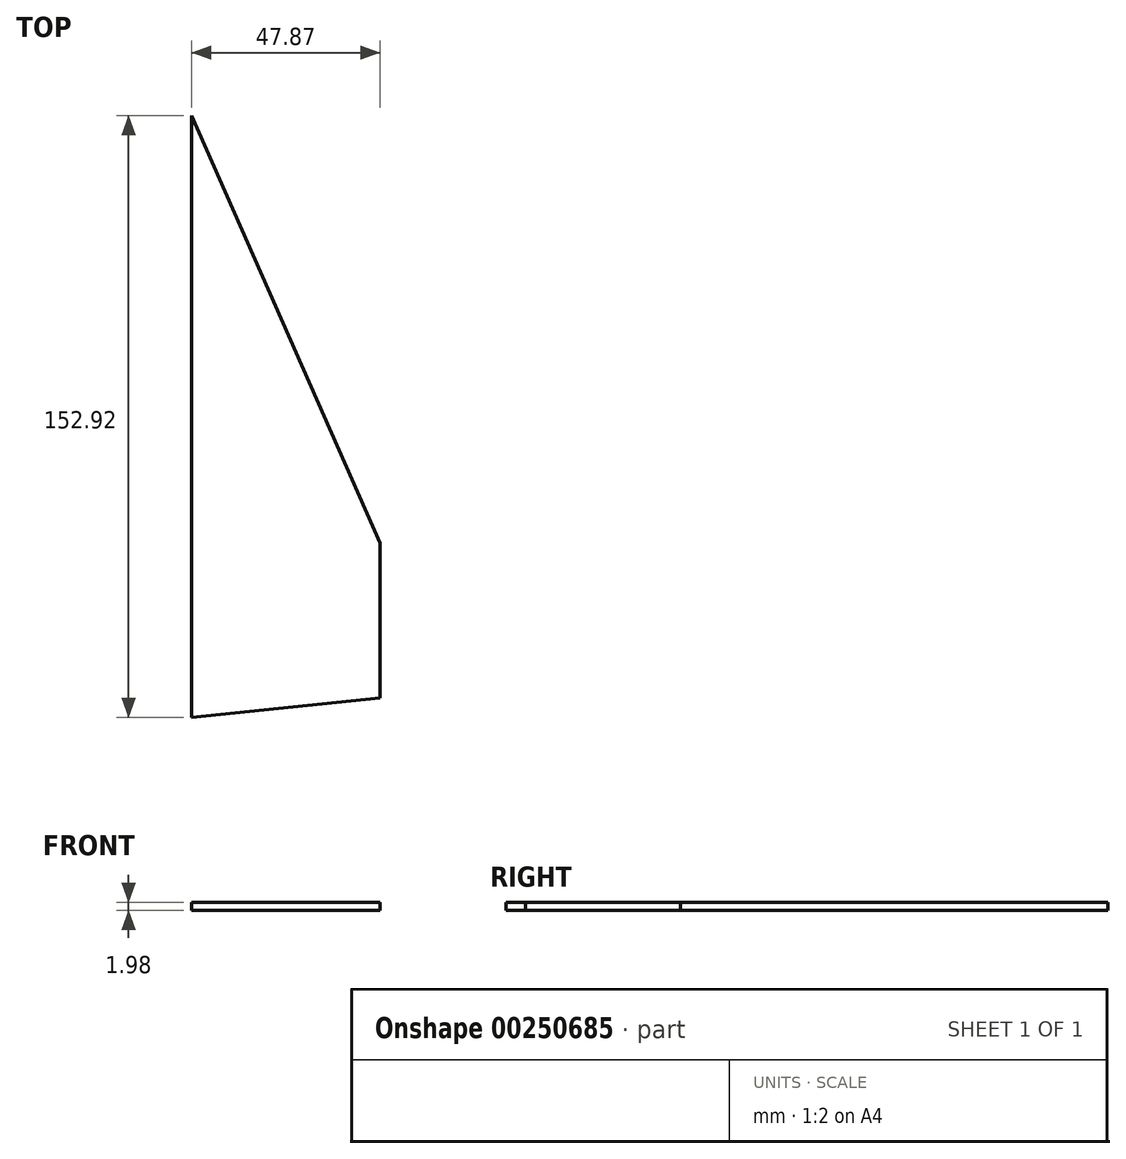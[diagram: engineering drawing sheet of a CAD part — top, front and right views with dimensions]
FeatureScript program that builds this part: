
annotation { "Feature Type Name" : "Feature", "Feature Type Description" : "" }
export const myFeature = defineFeature(function(context is Context, id is Id, definition is map)
    precondition{}
    {
        {
            var Q0;
            Q0=qCreatedBy(makeId("Top.planeOp"),FACE);
            var sketch = newSketch(context, id + "F0", { "sketchPlane" : qUnion([Q0])});
            skLineSegment(sketch, "E0", {"start": v(-66.6, -76.3) * mm, "end": v(-66.6, 76.6) * mm});
            skLineSegment(sketch, "E1", {"start": v(-66.6, 76.6) * mm, "end": v(-18.72, -31.91) * mm});
            skLineSegment(sketch, "E2", {"start": v(-18.72, -31.91) * mm, "end": v(-18.72, -71.37) * mm});
            skLineSegment(sketch, "E3", {"start": v(-18.72, -71.37) * mm, "end": v(-66.6, -76.3) * mm});
            skSolve(sketch);
        }
        {
            var Q0;
            Q0=makeQuery(id+"F0.imprint","IMPRINT",FACE,{"disambiguationData":[TD([[makeQuery(id+"F0.imprint","IMPRINT",EDGE,{"derivedFrom":sQuery(id+"F0.wireOp",EDGE,"E0")}),-1.0]])]});
            extrude(context, id + "F1", {"entities" : qUnion([Q0]), "depth" : 1.98 * mm});
        }
    });
